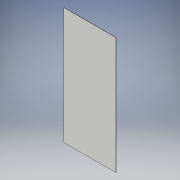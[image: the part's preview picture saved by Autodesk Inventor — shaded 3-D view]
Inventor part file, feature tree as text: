
AUTODESK INVENTOR PART (.ipt)
format: ipt  version: 2018 (Build 220112000, 112)  size: 90,624 bytes
history: native  units: in
note: dims shown in document units (in); Inventor stores cm internally (conversion verified against a paired STEP export)
features: extrude x1, sketch x1
ambient origin geometry x8: Origin, YZ Plane, XZ Plane, XY Plane, X Axis, Y Axis, Z Axis, Center Point
bodies: Solid1 (feature_tree)
feature tree (2):
  extrude  "Extrusion1"  Depth=19.0in
  sketch  "Sketch1"  dims[d0=8.5in d1=19.0in d2=0.0625in d3=0.0in]
